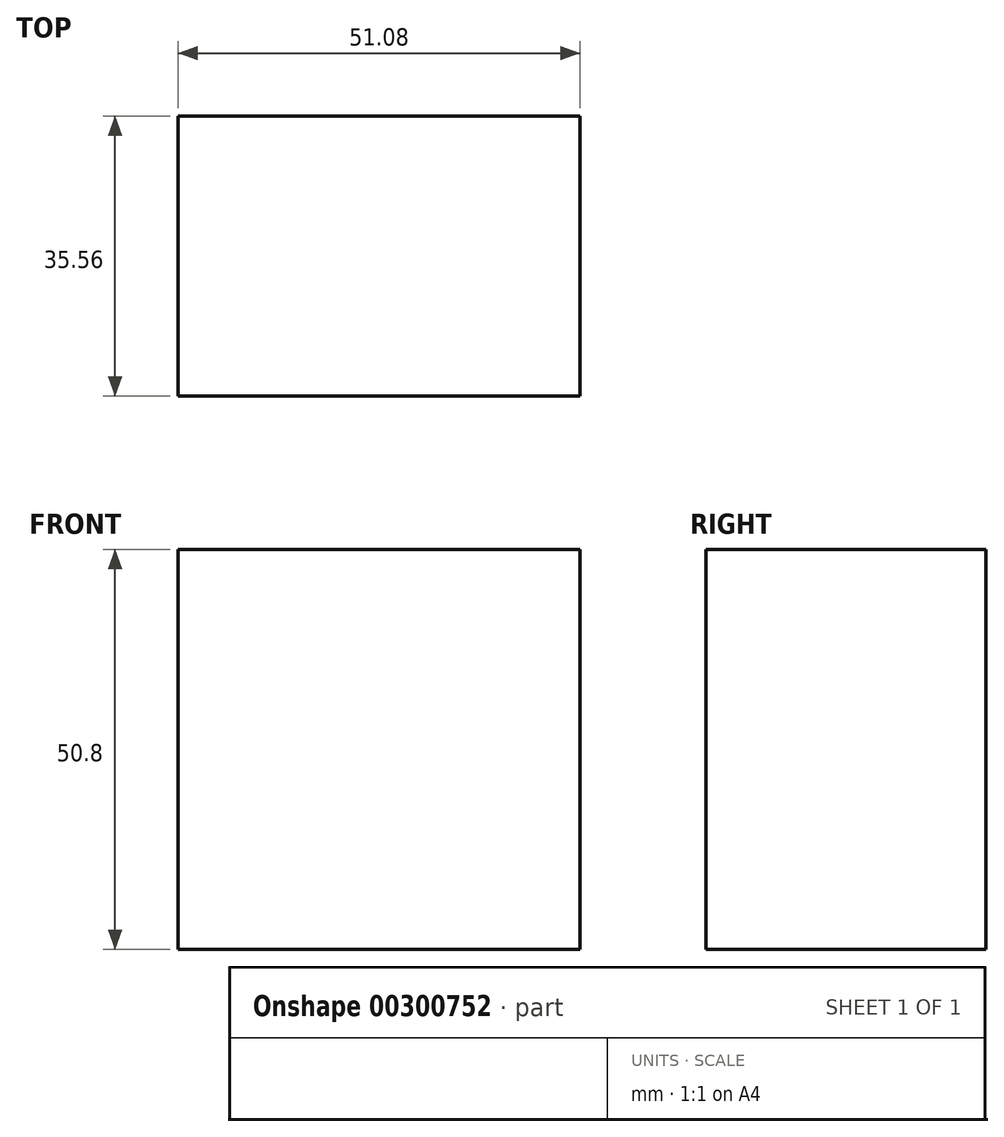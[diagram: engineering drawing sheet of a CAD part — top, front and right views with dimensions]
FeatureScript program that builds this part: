
annotation { "Feature Type Name" : "Feature", "Feature Type Description" : "" }
export const myFeature = defineFeature(function(context is Context, id is Id, definition is map)
    precondition{}
    {
        {
            var Q0;
            Q0=qCreatedBy(makeId("Front.planeOp"),FACE);
            var sketch = newSketch(context, id + "F0", { "sketchPlane" : qUnion([Q0])});
            skLineSegment(sketch, "E0.bottom", {"start": v(-28.07, -12.89) * mm, "end": v(23.01, -12.89) * mm});
            skLineSegment(sketch, "E0.top", {"start": v(-28.07, 37.91) * mm, "end": v(23.01, 37.91) * mm});
            skLineSegment(sketch, "E0.left", {"start": v(-28.07, -12.89) * mm, "end": v(-28.07, 37.91) * mm});
            skLineSegment(sketch, "E0.right", {"start": v(23.01, -12.89) * mm, "end": v(23.01, 37.91) * mm});
            skSolve(sketch);
        }
        {
            var Q0;
            Q0=makeQuery(id+"F0.imprint","IMPRINT",FACE,{"disambiguationData":[TD([[makeQuery(id+"F0.imprint","IMPRINT",EDGE,{"derivedFrom":sQuery(id+"F0.wireOp",EDGE,"E0.bottom")}),1.0]])]});
            extrude(context, id + "F1", {"entities" : qUnion([Q0]), "depth" : 35.56 * mm});
        }
    });
